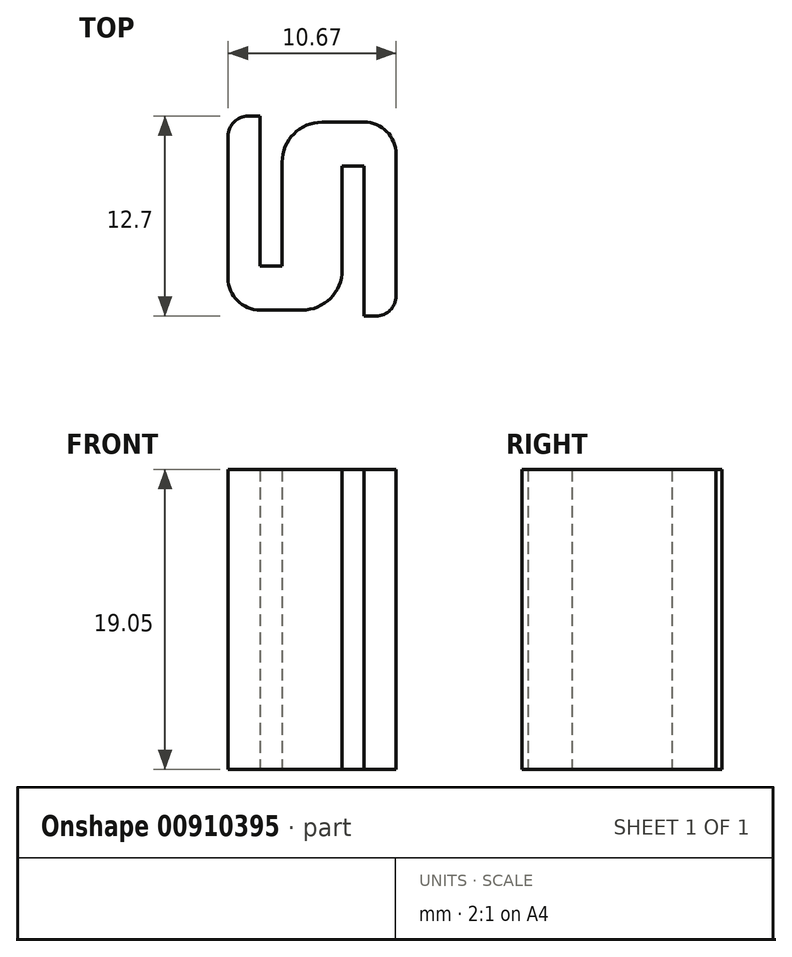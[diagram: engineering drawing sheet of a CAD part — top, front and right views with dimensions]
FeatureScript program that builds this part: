
annotation { "Feature Type Name" : "Feature", "Feature Type Description" : "" }
export const myFeature = defineFeature(function(context is Context, id is Id, definition is map)
    precondition{}
    {
        {
            var Q0;
            Q0=qCreatedBy(makeId("Top.planeOp"),FACE);
            var sketch = newSketch(context, id + "F0", { "sketchPlane" : qUnion([Q0])});
            skLineSegment(sketch, "E0", {"start": v(0, 9.52) * mm, "end": v(0, 0) * mm});
            skLineSegment(sketch, "E1", {"start": v(0, 0) * mm, "end": v(1.4, 0) * mm});
            skLineSegment(sketch, "E2", {"start": v(1.4, 0) * mm, "end": v(1.4, 6.6) * mm});
            skLineSegment(sketch, "E3", {"start": v(3.94, 9.14) * mm, "end": v(6.6, 9.14) * mm});
            skLineSegment(sketch, "E4", {"start": v(8.64, 7.11) * mm, "end": v(8.64, -1.9) * mm});
            skLineSegment(sketch, "E5", {"start": v(7.37, -3.17) * mm, "end": v(6.6, -3.17) * mm});
            skLineSegment(sketch, "E6", {"start": v(6.6, -3.17) * mm, "end": v(6.6, 6.35) * mm});
            skLineSegment(sketch, "E7", {"start": v(6.6, 6.35) * mm, "end": v(5.2, 6.35) * mm});
            skLineSegment(sketch, "E8", {"start": v(5.2, 6.35) * mm, "end": v(5.2, -0.25) * mm});
            skLineSegment(sketch, "E9", {"start": v(2.67, -2.8) * mm, "end": v(0, -2.8) * mm});
            skLineSegment(sketch, "E10", {"start": v(-2.03, -0.76) * mm, "end": v(-2.03, 8.25) * mm});
            skLineSegment(sketch, "E11", {"start": v(-0.76, 9.52) * mm, "end": v(0, 9.52) * mm});
            skPoint(sketch, "E12.visualSharp", {"position": v(1.4, 9.14) * mm});
            skArc(sketch, "E12.filletArc", {"start": v(3.94, 9.14) * mm, "mid": v(2.14, 8.4) * mm, "end": v(1.4, 6.6) * mm});
            skPoint(sketch, "E13.visualSharp", {"position": v(5.2, -2.8) * mm});
            skArc(sketch, "E13.filletArc", {"start": v(2.67, -2.8) * mm, "mid": v(4.46, -2.05) * mm, "end": v(5.2, -0.25) * mm});
            skPoint(sketch, "E14.visualSharp", {"position": v(8.64, 9.14) * mm});
            skArc(sketch, "E14.filletArc", {"start": v(8.64, 7.11) * mm, "mid": v(8.04, 8.55) * mm, "end": v(6.6, 9.14) * mm});
            skPoint(sketch, "E15.visualSharp", {"position": v(-2.03, -2.8) * mm});
            skArc(sketch, "E15.filletArc", {"start": v(-2.03, -0.76) * mm, "mid": v(-1.44, -2.2) * mm, "end": v(0, -2.8) * mm});
            skPoint(sketch, "E16.visualSharp", {"position": v(-2.03, 9.53) * mm});
            skArc(sketch, "E16.filletArc", {"start": v(-0.76, 9.52) * mm, "mid": v(-1.66, 9.15) * mm, "end": v(-2.03, 8.25) * mm});
            skPoint(sketch, "E17.visualSharp", {"position": v(8.64, -3.17) * mm});
            skArc(sketch, "E17.filletArc", {"start": v(7.37, -3.17) * mm, "mid": v(8.26, -2.8) * mm, "end": v(8.64, -1.9) * mm});
            skSolve(sketch);
        }
        {
            var Q0;
            Q0 = qSketchRegion(id + "F0", true);
            extrude(context, id + "F1", {"entities" : qUnion([Q0]), "depth" : 19.05 * mm, "offsetDistance" : 25.4 * mm});
        }
    });
